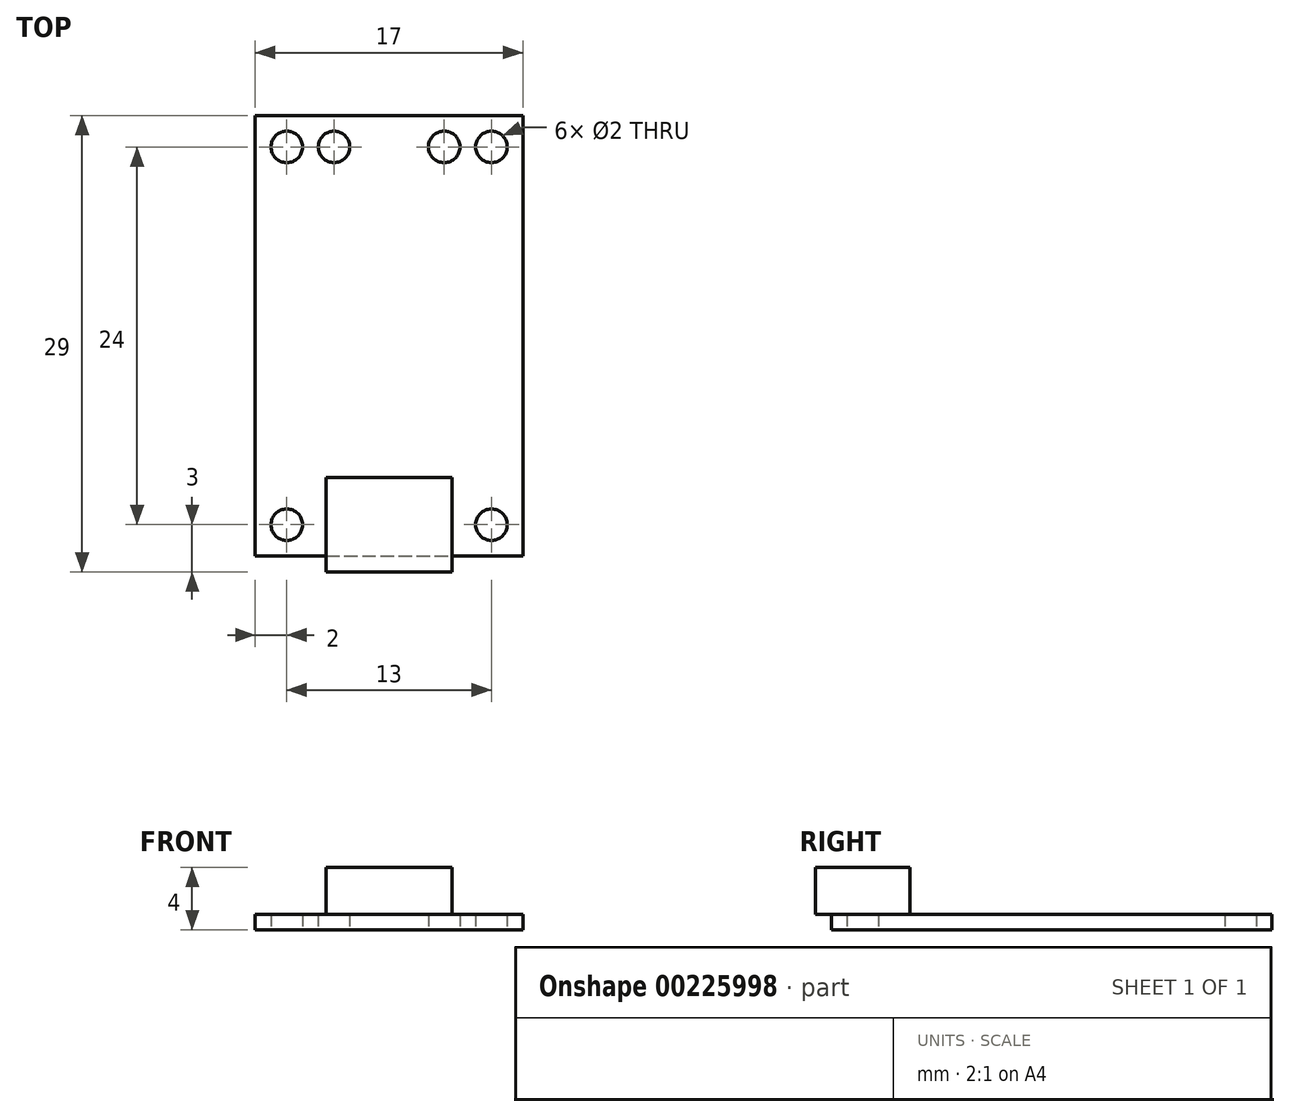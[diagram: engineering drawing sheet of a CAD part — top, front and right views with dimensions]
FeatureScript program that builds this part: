
annotation { "Feature Type Name" : "Feature", "Feature Type Description" : "" }
export const myFeature = defineFeature(function(context is Context, id is Id, definition is map)
    precondition{}
    {
        {
            var Q0;
            Q0=qCreatedBy(makeId("Top.planeOp"),FACE);
            var sketch = newSketch(context, id + "F0", { "sketchPlane" : qUnion([Q0])});
            skLineSegment(sketch, "E0.bottom", {"start": v(0, 0) * mm, "end": v(17, 0) * mm});
            skLineSegment(sketch, "E0.top", {"start": v(0, 28) * mm, "end": v(17, 28) * mm});
            skLineSegment(sketch, "E0.left", {"start": v(0, 0) * mm, "end": v(0, 28) * mm});
            skLineSegment(sketch, "E0.right", {"start": v(17, 0) * mm, "end": v(17, 28) * mm});
            skCircle(sketch, "E1", {"center": v(2, 2) * mm, "radius": 1 * mm});
            skLineSegment(sketch, "E2", {"start": v(8.5, 28) * mm, "end": v(8.5, 0) * mm, "construction": true});
            skCircle(sketch, "E3", {"center": v(2, 26) * mm, "radius": 1 * mm});
            skCircle(sketch, "E4", {"center": v(5, 26) * mm, "radius": 1 * mm});
            skCircle(sketch, "E5.MirrorC", {"center": v(12, 26) * mm, "radius": 1 * mm});
            skCircle(sketch, "E6.MirrorC", {"center": v(15, 26) * mm, "radius": 1 * mm});
            skCircle(sketch, "E7.MirrorC", {"center": v(15, 2) * mm, "radius": 1 * mm});
            skSolve(sketch);
        }
        {
            var Q0;
            Q0 = qSketchRegion(id + "F0", true);
            extrude(context, id + "F1", {"entities" : qUnion([Q0]), "depth" : 1 * mm, "offsetDistance" : 25 * mm});
        }
        {
            var Q0;
            Q0=makeQuery(id+"F1.opExtrude","CAP_FACE",FACE,{"disambiguationData":[OSD([sQuery(id+"F0.wireOp",EDGE,"E0.bottom"),sQuery(id+"F0.wireOp",EDGE,"E0.top"),sQuery(id+"F0.wireOp",EDGE,"E0.left"),sQuery(id+"F0.wireOp",EDGE,"E0.right"),sQuery(id+"F0.wireOp",EDGE,"E1"),sQuery(id+"F0.wireOp",EDGE,"E3"),sQuery(id+"F0.wireOp",EDGE,"E4"),sQuery(id+"F0.wireOp",EDGE,"E5.MirrorC"),sQuery(id+"F0.wireOp",EDGE,"E6.MirrorC"),sQuery(id+"F0.wireOp",EDGE,"E7.MirrorC")])],"isStart":false});
            var sketch = newSketch(context, id + "F2", { "sketchPlane" : qUnion([Q0])});
            skLineSegment(sketch, "E8.bottom", {"start": v(4.5, -1) * mm, "end": v(12.5, -1) * mm});
            skLineSegment(sketch, "E8.top", {"start": v(4.5, 5) * mm, "end": v(12.5, 5) * mm});
            skLineSegment(sketch, "E8.left", {"start": v(4.5, -1) * mm, "end": v(4.5, 5) * mm});
            skLineSegment(sketch, "E8.right", {"start": v(12.5, -1) * mm, "end": v(12.5, 5) * mm});
            skLineSegment(sketch, "E9", {"start": v(8.5, 5) * mm, "end": v(8.5, -1) * mm, "construction": true});
            skLineSegment(sketch, "E10", {"start": v(8.5, 28) * mm, "end": v(8.5, 0) * mm, "construction": true});
            skSolve(sketch);
        }
        {
            var Q0;
            Q0 = qSketchRegion(id + "F2", true);
            extrude(context, id + "F3", {"entities" : qUnion([Q0]), "operationType" : NewBodyOperationType.ADD, "depth" : 3 * mm, "offsetDistance" : 25 * mm});
        }
    });
